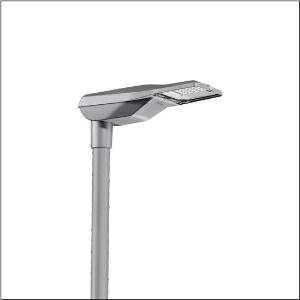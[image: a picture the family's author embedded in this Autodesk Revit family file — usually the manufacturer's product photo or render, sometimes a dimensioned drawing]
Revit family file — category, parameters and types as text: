
# Revit family: streetlight_sl_21_iq_micro___st1_5a_5xe1p41d08db_9421
name_source: partatom
category: Lighting Fixtures
units: mm (PartAtom-declared; Revit-internal decimal feet)

## family parameters
Cut with Voids When Loaded = No
Host = Face
Light Source = No
Part Type = Normal
Room Calculation Point = No
Round Connector Dimension = Use Diameter
Shared = No

## types (1)
- --- (1 x LED, 4930 lm, 36.4 W, 4000K)
    Apparent Load = 36 VA
    CIE Flux Codes = 22 53 95 100 100
    Color Rendering = 70
    Color Temperature = 4000K
    Default Elevation = 1800 mm
    Description = Streetlight SL 21 iQ micro, mast luminaire, primary light control with lens, of PMMA, primary optical cover: cover, of toughened safety glass, transparent, light distribution: ST1.5a, light emission: direct distribution, primary light characteristic: asymmetric, installation type: post-top, side-entry, LED, High Power LED, rated luminous flux: 4.930lm, luminous efficacy: 135lm/W, light colour: 740, colour temperature: 4000K, control: Auto-Match, Temp-Guard, Lumen-Switch, Night-Set, Smart-Wire, Light-Fading, Desk-Remote (wireless, voltage-free reading and setting of iQ features in the workshop via application-optimized NFC function/RFID function), optimised constant luminous flux control (CLO 2.0), presetting dimming linear, mains connection: 220..240V, AC, 50/60Hz, start of lifetime: 36W, end of service life: 38W, reduction: 16W, luminaire housing, of diecast aluminium, powder-coated, Siteco® metallic grey (DB 702S), corrosivity category C5 mid according to DIN EN ISO 12944, please order mast flange separately, inclination adjustable: 0°, 5°, 10°, 15°, sealing non-destructively replaceable, multi-level sealing system, length: 528mm, width: 235mm, height: 110mm, mast flange for spigot size: 42mm (side-entry): 5XC10008XM4, 60/48mm (side-entry/post-top): 5XC10108XM2, 76/60mm (side-entry/post-top): 5XC10108XM1, protection rating (complete): IP66, insulation class (complete): insulation class II (safety insulation), certification: CE, ENEC, ENEC+, VDE, impact resistance: IK09, permissible operating ambient temperature for outdoor applications: -40..+50°C, standard-compliant lighting for roads and squares, packaging unit: 1 piece

Light Distribution: ST1.5a
    Height = 110 mm
    Lamp = 1 x LED
    Lamp Light Flux = 4930 lm
    Lamp Power = 36.4 W
    Lamp count = 1
    Length = 528 mm
    Luminous efficacy = 135 lm/W
    Manufacturer = Siteco
    ModVariant = No
    Model = 5XE1P41D08DB
    Number of Poles = 1
    OnlyDefault = Yes
    Power Factor = 1
    Product Name = Streetlight SL 21 iQ micro | ST1.5a
    Product group = mast luminaire | pylon top
    ProductGroupID = 6100
    Protection Class = Protection class II
    Protection Degree = IP 66
    RLX_Detail_Level = 1
    RLX_Emergency_Light_Flux = 0 lm
    RLX_Emergency_Type = 0
    RLX_Emergency_Type_DB = No
    RlxData = <blob elided: 103201 chars, md5=048d20ba>
    Socket = socket
    Standby Power = 0 W
    System Light Flux = 4930 lm
    System Power = 36 W
    Type Comments = factory setting: luminous flux: 100 % | dim-lin: 254 | 715 mA
    Type Image = l_1006881.jpg
    URL = http://relux.com
    VarID = @adj_086129
    Voltage = 0 V
    Weight = 0.00 kg
    Width = 235 mm

## geometry (parser evidence)
native form markers: Blend x4, Sweep x10
no freeform markers — native parametric forms only
